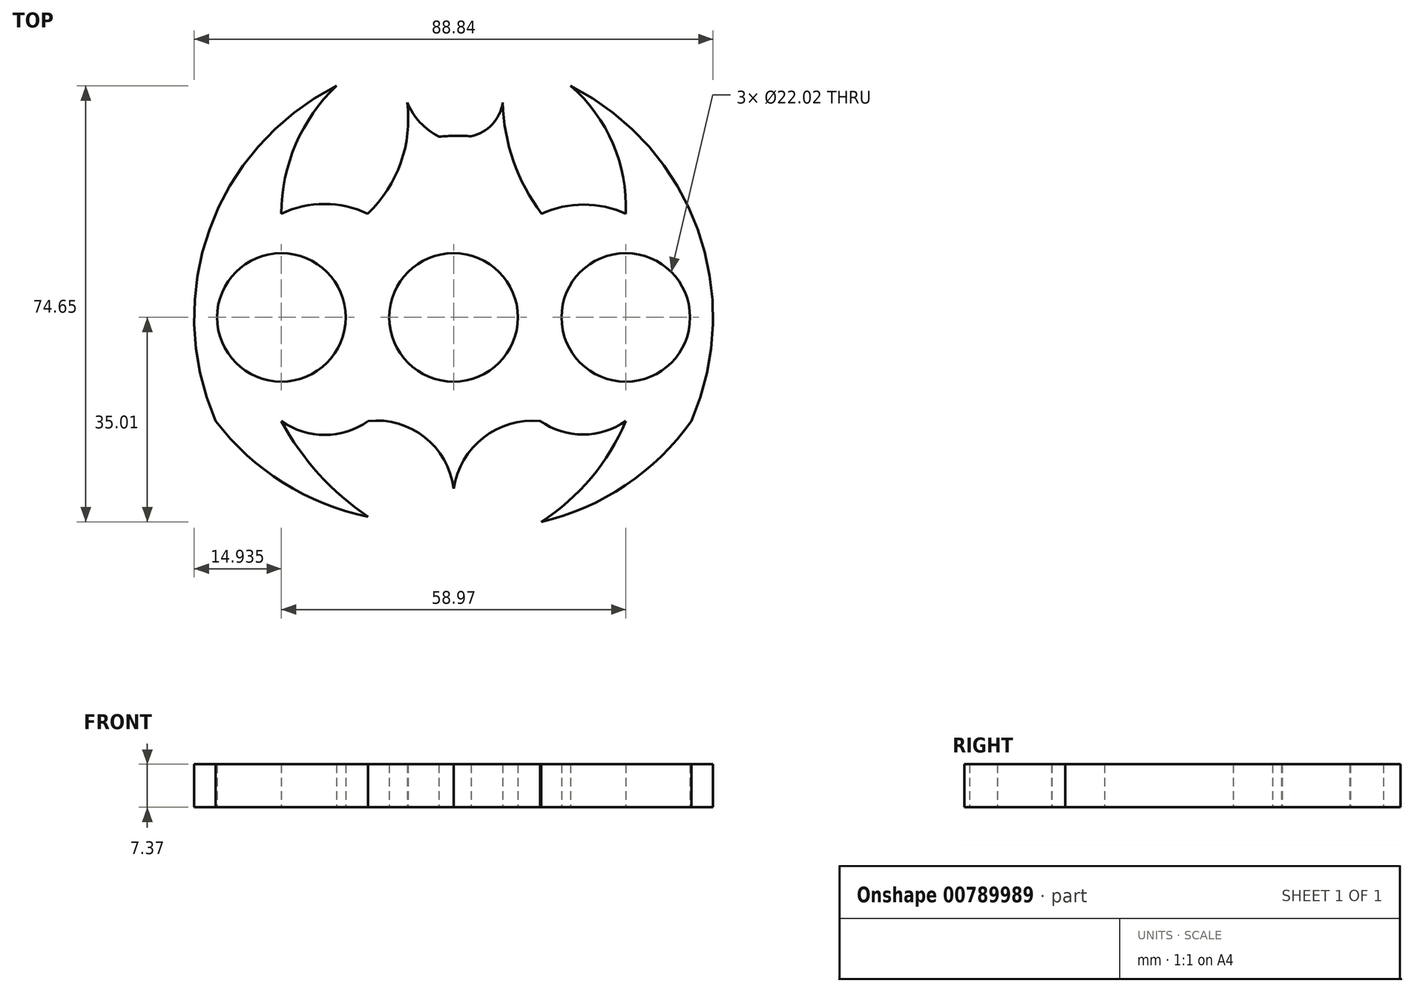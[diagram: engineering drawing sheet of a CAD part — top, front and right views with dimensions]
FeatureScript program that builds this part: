
annotation { "Feature Type Name" : "Feature", "Feature Type Description" : "" }
export const myFeature = defineFeature(function(context is Context, id is Id, definition is map)
    precondition{}
    {
        {
            var Q0;
            Q0=qCreatedBy(makeId("Top.planeOp"),FACE);
            var sketch = newSketch(context, id + "F0", { "sketchPlane" : qUnion([Q0])});
            skCircle(sketch, "E0", {"center": v(0, 0) * mm, "radius": 11.01 * mm});
            skCircle(sketch, "E1", {"center": v(-29.49, 0) * mm, "radius": 11.01 * mm});
            skCircle(sketch, "E2", {"center": v(29.49, 0) * mm, "radius": 11.01 * mm});
            skArc(sketch, "E3", {"start": v(40.72, -17.75) * mm, "mid": v(41.8, 15.05) * mm, "end": v(20.05, 39.64) * mm});
            skArc(sketch, "E4", {"start": v(2.98, 31) * mm, "mid": v(0.23, 31.1) * mm, "end": v(-2.51, 30.93) * mm});
            skArc(sketch, "E5", {"start": v(2.98, 31) * mm, "mid": v(6.6, 33.04) * mm, "end": v(8.42, 36.77) * mm});
            skArc(sketch, "E6", {"start": v(-7.95, 36.77) * mm, "mid": v(-5.73, 33.38) * mm, "end": v(-2.51, 30.93) * mm});
            skArc(sketch, "E7", {"start": v(-14.71, 17.77) * mm, "mid": v(-9.05, 26.46) * mm, "end": v(-7.95, 36.77) * mm});
            skArc(sketch, "E8", {"start": v(-20.05, 39.64) * mm, "mid": v(-27, 29.67) * mm, "end": v(-29.49, 17.77) * mm});
            skArc(sketch, "E9", {"start": v(29.49, 17.77) * mm, "mid": v(27.27, 29.78) * mm, "end": v(20.05, 39.64) * mm});
            skArc(sketch, "E10", {"start": v(8.42, 36.77) * mm, "mid": v(10.25, 26.74) * mm, "end": v(15.1, 17.77) * mm});
            skArc(sketch, "E11", {"start": v(-14.71, 17.77) * mm, "mid": v(-22.1, 19.42) * mm, "end": v(-29.49, 17.77) * mm});
            skArc(sketch, "E12", {"start": v(29.49, 17.77) * mm, "mid": v(22.29, 19.3) * mm, "end": v(15.1, 17.77) * mm});
            skArc(sketch, "E13", {"start": v(14.99, -35) * mm, "mid": v(23.55, -27.49) * mm, "end": v(29.49, -17.75) * mm});
            skArc(sketch, "E14", {"start": v(-29.49, -17.75) * mm, "mid": v(-23.07, -26.84) * mm, "end": v(-14.65, -34.11) * mm});
            skLineSegment(sketch, "E15", {"start": v(0, -29.34) * mm, "end": v(0, -24.33) * mm});
            skArc(sketch, "E16", {"start": v(0, -29.34) * mm, "mid": v(-4.94, -20.53) * mm, "end": v(-14.64, -17.75) * mm});
            skArc(sketch, "E17", {"start": v(14.84, -17.75) * mm, "mid": v(5.1, -20.58) * mm, "end": v(0, -29.34) * mm});
            skArc(sketch, "E18", {"start": v(-29.49, -17.75) * mm, "mid": v(-22.06, -20.12) * mm, "end": v(-14.64, -17.75) * mm});
            skArc(sketch, "E19", {"start": v(14.84, -17.75) * mm, "mid": v(22.16, -20.05) * mm, "end": v(29.49, -17.75) * mm});
            skArc(sketch, "E20", {"start": v(14.99, -35) * mm, "mid": v(29.44, -28.75) * mm, "end": v(40.72, -17.75) * mm});
            skArc(sketch, "E21", {"start": v(-40.72, -17.75) * mm, "mid": v(-29.18, -28.31) * mm, "end": v(-14.65, -34.11) * mm});
            skPoint(sketch, "E22.orphan", {"position": v(0, -40.56) * mm});
            skArc(sketch, "E23.trimOffspring", {"start": v(-20.05, 39.64) * mm, "mid": v(-41.8, 15.05) * mm, "end": v(-40.72, -17.75) * mm});
            skSolve(sketch);
        }
        {
            var Q0;
            Q0 = qSketchRegion(id + "F0", true);
            extrude(context, id + "F1", {"entities" : qUnion([Q0]), "depth" : 7.37 * mm, "offsetDistance" : 25.4 * mm});
        }
    });
